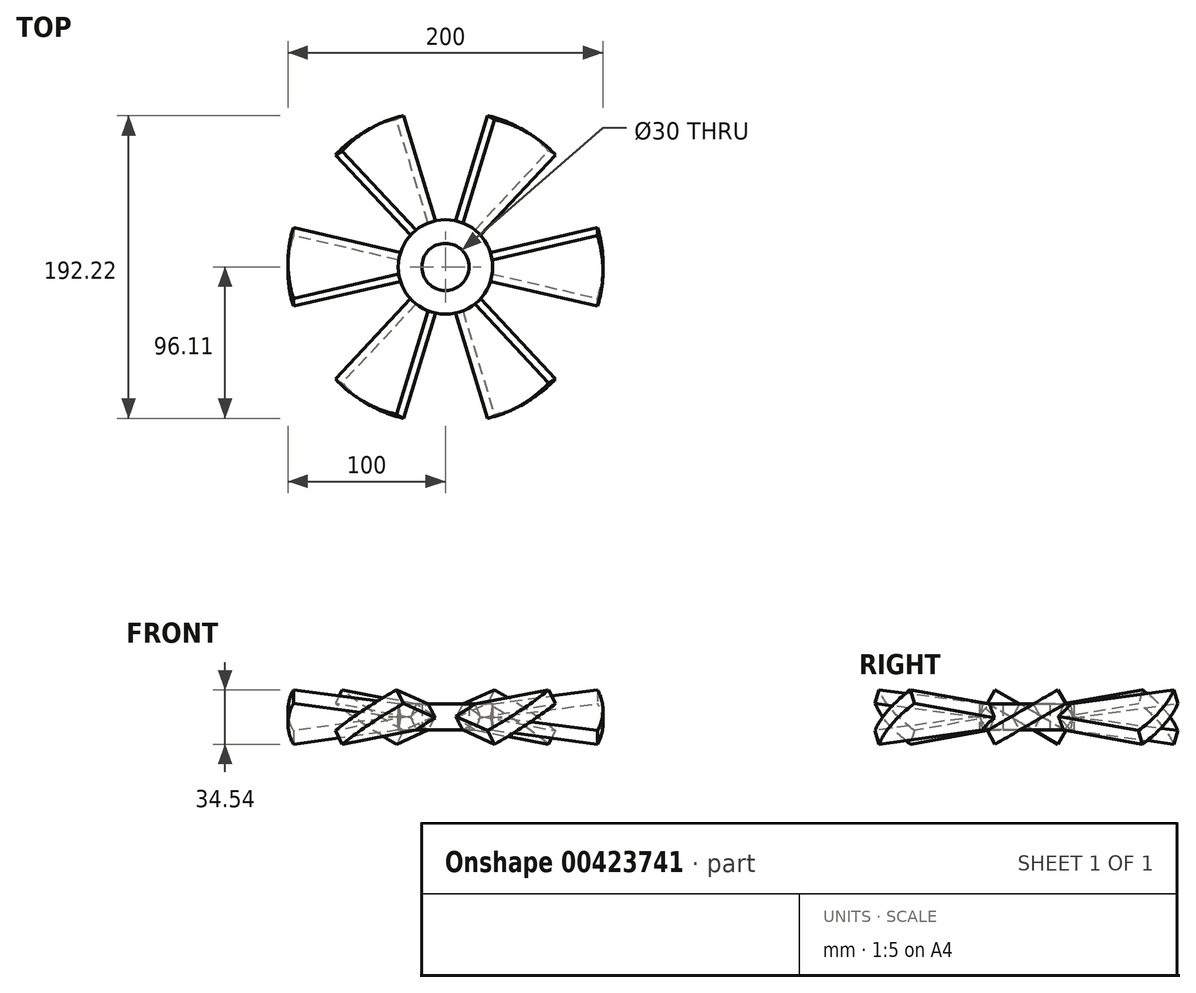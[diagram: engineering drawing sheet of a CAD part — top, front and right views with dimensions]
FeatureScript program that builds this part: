
annotation { "Feature Type Name" : "Feature", "Feature Type Description" : "" }
export const myFeature = defineFeature(function(context is Context, id is Id, definition is map)
    precondition{}
    {
        {
            var Q0;
            Q0=qCreatedBy(makeId("Top.planeOp"),FACE);
            var sketch = newSketch(context, id + "F0", { "sketchPlane" : qUnion([Q0])});
            skCircle(sketch, "E0", {"center": v(0, 0) * mm, "radius": 30 * mm});
            skArc(sketch, "E1", {"start": v(96.6, -25.88) * mm, "mid": v(100, 0) * mm, "end": v(96.6, 25.88) * mm});
            skLineSegment(sketch, "E2", {"start": v(28.98, 7.76) * mm, "end": v(96.6, 25.88) * mm});
            skCircle(sketch, "E3", {"center": v(0, 0) * mm, "radius": 15 * mm});
            skLineSegment(sketch, "E4", {"start": v(28.98, 7.76) * mm, "end": v(22.74, 6.1) * mm});
            skLineSegment(sketch, "E5.MirrorCS", {"start": v(28.98, -7.76) * mm, "end": v(96.6, -25.88) * mm});
            skLineSegment(sketch, "E6.MirrorCS", {"start": v(28.98, -7.76) * mm, "end": v(22.74, -6.1) * mm});
            skArc(sketch, "E7", {"start": v(22.74, -6.1) * mm, "mid": v(23.55, 0) * mm, "end": v(22.74, 6.1) * mm});
            skSolve(sketch);
        }
        {
            var Q0;
            Q0=makeQuery(id+"F0.imprint","IMPRINT",FACE,{"disambiguationData":[TD([[makeQuery(id+"F0.imprint","IMPRINT",EDGE,{"derivedFrom":sQuery(id+"F0.wireOp",EDGE,"E1")}),1.0]])]});
            var Q1;
            {var subQ0=sQuery(id+"F0.wireOp",EDGE,"E4");Q1=makeQuery(id+"F0.imprint","IMPRINT",FACE,{"disambiguationData":[TD([[makeQuery(id+"F0.imprint","IMPRINT",EDGE,{"derivedFrom":subQ0}),1.0]])]});}
            extrude(context, id + "F1", {"entities" : qUnion([Q0, Q1]), "depth" : 5 * mm, "hasSecondDirection" : true, "secondDirectionOppositeDirection" : true, "secondDirectionDepth" : 5 * mm});
        }
        {
            var Q0;
            Q0=qCreatedBy(makeId("Top.planeOp"),FACE);
            var sketch = newSketch(context, id + "F2", { "sketchPlane" : qUnion([Q0])});
            skLineSegment(sketch, "E8", {"start": v(-59.76, 0) * mm, "end": v(34.97, 0) * mm});
            skSolve(sketch);
        }
        {
            var Q0;
            Q0=makeQuery(id+"F1.opExtrude","SWEPT_BODY",BODY,{"disambiguationData":[OSD([sQuery(id+"F0.wireOp",EDGE,"E0"),sQuery(id+"F0.wireOp",EDGE,"E1"),sQuery(id+"F0.wireOp",EDGE,"E2"),sQuery(id+"F0.wireOp",EDGE,"ee382824-093d-4231-ac3c-0c521fdb87710.MirrorCS")])]});
            var Q1;
            Q1=sQuery(id+"F2.wireOp",EDGE,"E8");
            transform(context, id + "F3", {"entities" : qUnion([Q0]), "transformType" : TransformType.ROTATION, "transformAxis" : qUnion([Q1]), "angle" : 30 * degree, "makeCopy" : false});
        }
        {
            var Q0;
            Q0=qCreatedBy(makeId("Top.planeOp"),FACE);
            var sketch = newSketch(context, id + "F4", { "sketchPlane" : qUnion([Q0])});
            skCircle(sketch, "E9", {"center": v(0, 0) * mm, "radius": 15 * mm});
            skCircle(sketch, "E10", {"center": v(0, 0) * mm, "radius": 30 * mm});
            skSolve(sketch);
        }
        {
            var Q0;
            Q0=makeQuery(id+"F4.imprint","IMPRINT",FACE,{"disambiguationData":[TD([[makeQuery(id+"F4.imprint","IMPRINT",EDGE,{"derivedFrom":sQuery(id+"F4.wireOp",EDGE,"E9")}),-1.0]])]});
            extrude(context, id + "F5", {"entities" : qUnion([Q0]), "operationType" : NewBodyOperationType.REMOVE, "oppositeDirection" : true, "depth" : 25 * mm, "hasSecondDirection" : true, "secondDirectionOppositeDirection" : false, "secondDirectionDepth" : 25 * mm});
        }
        {
            var Q0;
            Q0=makeQuery(id+"F0.imprint","IMPRINT",FACE,{"disambiguationData":[TD([[makeQuery(id+"F0.imprint","IMPRINT",EDGE,{"derivedFrom":sQuery(id+"F0.wireOp",EDGE,"E3")}),-1.0]])]});
            var Q1;
            {var subQ0=sQuery(id+"F0.wireOp",EDGE,"E4");Q1=makeQuery(id+"F0.imprint","IMPRINT",FACE,{"disambiguationData":[TD([[makeQuery(id+"F0.imprint","IMPRINT",EDGE,{"derivedFrom":subQ0}),1.0]])]});}
            var Q2;
            {var subQ0=sQuery(id+"F0.wireOp",EDGE,"E4");var subQ1=sQuery(id+"F0.wireOp",EDGE,"E2");Q2=makeQuery(id+"F5.boolean.opBoolean","INTERSECT",VERTEX,{"derivedFrom":[makeQuery(id+"F1.opExtrude","CAP_FACE",FACE,{"disambiguationData":[OSD([sQuery(id+"F0.wireOp",EDGE,"E1"),subQ1,subQ0,sQuery(id+"F0.wireOp",EDGE,"E5.MirrorCS"),sQuery(id+"F0.wireOp",EDGE,"E6.MirrorCS"),sQuery(id+"F0.wireOp",EDGE,"E7")])],"isStart":false}),makeQuery(id+"F1.opExtrude","SWEPT_FACE",FACE,{"disambiguationData":[OSD([subQ1,subQ0])]}),makeQuery(id+"F5.opExtrude","SWEPT_FACE",FACE,{"disambiguationData":[OSD([sQuery(id+"F4.wireOp",EDGE,"E10")])]})]});}
            var Q3;
            {var subQ0=sQuery(id+"F0.wireOp",EDGE,"E6.MirrorCS");var subQ1=sQuery(id+"F0.wireOp",EDGE,"E5.MirrorCS");Q3=makeQuery(id+"F5.boolean.opBoolean","INTERSECT",VERTEX,{"derivedFrom":[makeQuery(id+"F1.opExtrude","CAP_FACE",FACE,{"disambiguationData":[OSD([sQuery(id+"F0.wireOp",EDGE,"E1"),sQuery(id+"F0.wireOp",EDGE,"E2"),sQuery(id+"F0.wireOp",EDGE,"E4"),subQ1,subQ0,sQuery(id+"F0.wireOp",EDGE,"E7")])],"isStart":true}),makeQuery(id+"F1.opExtrude","SWEPT_FACE",FACE,{"disambiguationData":[OSD([subQ1,subQ0])]}),makeQuery(id+"F5.opExtrude","SWEPT_FACE",FACE,{"disambiguationData":[OSD([sQuery(id+"F4.wireOp",EDGE,"E10")])]})]});}
            extrude(context, id + "F6", {"entities" : qUnion([Q0, Q1]), "endBound" : BoundingType.UP_TO_VERTEX, "endBoundEntityVertex" : qUnion([Q2]), "depth" : 25 * mm, "hasSecondDirection" : true, "secondDirectionBound" : SecondDirectionBoundingType.UP_TO_VERTEX, "secondDirectionOppositeDirection" : true, "secondDirectionBoundEntityVertex" : qUnion([Q3]), "secondDirectionDepth" : 25 * mm});
        }
        {
            var Q0;
            Q0=makeQuery(id+"F1.opExtrude","SWEPT_BODY",BODY,{"disambiguationData":[OSD([sQuery(id+"F0.wireOp",EDGE,"E1"),sQuery(id+"F0.wireOp",EDGE,"E2"),sQuery(id+"F0.wireOp",EDGE,"E4"),sQuery(id+"F0.wireOp",EDGE,"E5.MirrorCS"),sQuery(id+"F0.wireOp",EDGE,"E6.MirrorCS"),sQuery(id+"F0.wireOp",EDGE,"E7")])]});
            var Q1;
            Q1=makeQuery(id+"F6.opExtrude","SWEPT_FACE",FACE,{"disambiguationData":[OSD([sQuery(id+"F0.wireOp",EDGE,"E0")])]});
            circularPattern(context, id + "F7", {"entities" : qUnion([Q0]), "axis" : qUnion([Q1]), "angle" : 360 * degree, "instanceCount" : 6, "equalSpace" : true});
        }
    });
